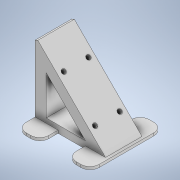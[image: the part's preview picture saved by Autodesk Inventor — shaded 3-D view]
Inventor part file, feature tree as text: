
AUTODESK INVENTOR PART (.ipt)
format: ipt  version: 2020 (Build 240168000, 168)  size: 215,040 bytes
history: native  units: in
note: dims shown in document units (in); Inventor stores cm internally (conversion verified against a paired STEP export)
features: extrude x5, sketch x5, fillet x3, chamfer x1
ambient origin geometry x8: Origin, YZ Plane, XZ Plane, XY Plane, X Axis, Y Axis, Z Axis, Center Point
bodies: Solid1 (feature_tree)
feature tree (14):
  extrude  "Extrusion1"  Depth=3.1496in
  extrude  "Extrusion2"  Depth=1.5748in TaperAngle=0.0deg
  fillet  "Fillet1"  Radius=1.063in
  extrude  "Extrusion3"  Depth=0.1654in
  extrude  "Extrusion4"  Depth=1.063in
  chamfer  "Chamfer1"  Distance=0.1654in
  fillet  "Fillet2"  Radius=1.9094in
  extrude  "Extrusion5"  Depth=0.3937in TaperAngle=0.0deg
  fillet  "Fillet3"  Radius=0.0157in
  sketch  "Sketch1"  dims[d0=3.1496in d1=3.1496in]
  sketch  "Sketch2"  dims[d2=45.0deg d3=1.5748in d4=0.0in d5=1.063in]
  sketch  "Sketch3"  dims[d6=0.1654in d7=0.1654in]
  sketch  "Sketch4"  dims[d8=0.2559in d10=1.063in]
  sketch  "Sketch5"  dims[d11=0.1654in d12=0.1654in d13=1.9094in d14=0.3937in d15=0.0in d16=0.0157in d17=0.4724in d18=0.315in d19=1.5748in d20=0.0in d21=3.937in d22=0.0in d23=0.7874in d24=0.7874in d25=1.1811in d26=1.1811in d27=0.1181in d28=0.0in d29=1.378in d30=1.378in d31=1.9094in d32=0.2559in d33=0.1575in d34=0.0787in d35=45.0deg d36=0.3937in d37=0.7874in d38=0.7874in d39=0.0in d40=3.1496in d41=0.9843in d42=0.9843in d43=0.1181in d44=0.0in d45=0.3937in]
